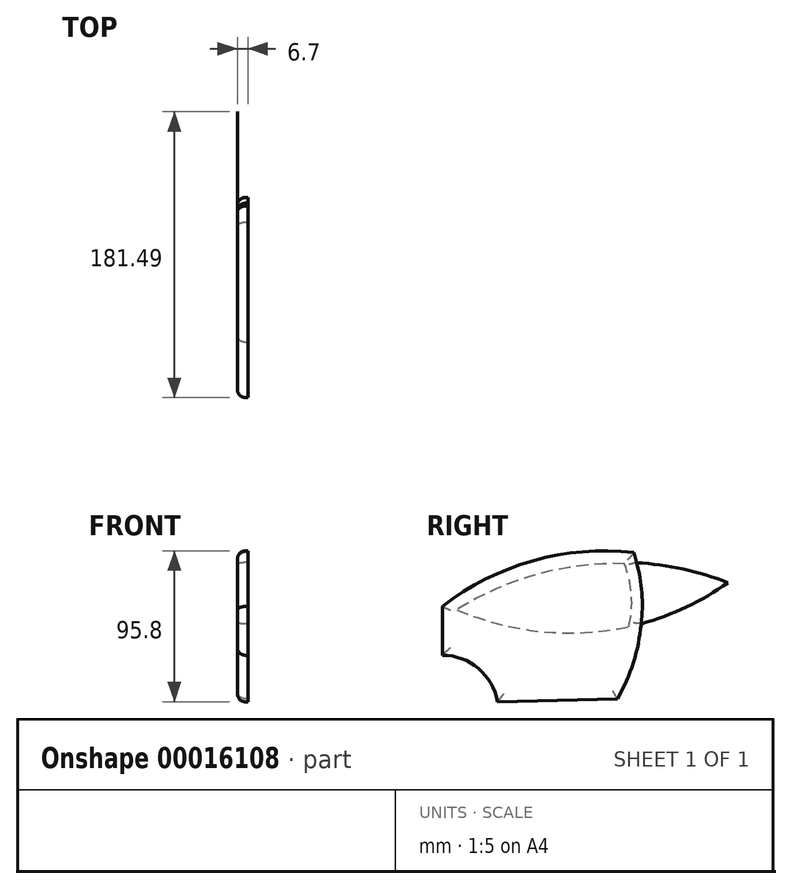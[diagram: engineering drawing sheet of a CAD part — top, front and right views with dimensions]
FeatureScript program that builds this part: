
annotation { "Feature Type Name" : "Feature", "Feature Type Description" : "" }
export const myFeature = defineFeature(function(context is Context, id is Id, definition is map)
    precondition{}
    {
        {
            var Q0;
            Q0=qCreatedBy(makeId("Right.planeOp"),FACE);
            var sketch = newSketch(context, id + "F0", { "sketchPlane" : qUnion([Q0])});
            skArc(sketch, "E0", {"start": v(39.4, 40.65) * mm, "mid": v(-24.74, 35.47) * mm, "end": v(-82.2, 6.49) * mm});
            skArc(sketch, "E1", {"start": v(-47.13, -54.09) * mm, "mid": v(-59.3, -32.92) * mm, "end": v(-82.2, -24.48) * mm});
            skLineSegment(sketch, "E2", {"start": v(-82.2, 6.94) * mm, "end": v(-82.2, -24.48) * mm});
            skLineSegment(sketch, "E3", {"start": v(-47.13, -54.09) * mm, "end": v(29.03, -52.2) * mm});
            skArc(sketch, "E4", {"start": v(29.03, -52.2) * mm, "mid": v(39.1, -29.18) * mm, "end": v(44.1, -4.55) * mm});
            skArc(sketch, "E5", {"start": v(41.16, 34.32) * mm, "mid": v(40.37, 37.5) * mm, "end": v(39.4, 40.65) * mm});
            skArc(sketch, "E6", {"start": v(44.1, -4.55) * mm, "mid": v(44.55, 15.03) * mm, "end": v(41.16, 34.32) * mm});
            skSolve(sketch);
        }
        {
            var Q0;
            Q0=qCreatedBy(makeId("Right.planeOp"),FACE);
            var sketch = newSketch(context, id + "F1", { "sketchPlane" : qUnion([Q0])});
            skArc(sketch, "E7", {"start": v(33.51, 33.61) * mm, "mid": v(-21.9, 26.86) * mm, "end": v(-72.98, 4.39) * mm});
            skArc(sketch, "E8", {"start": v(-72.98, 4.39) * mm, "mid": v(-19.22, -9.5) * mm, "end": v(36.21, -6.46) * mm});
            skArc(sketch, "E9", {"start": v(36.21, -6.46) * mm, "mid": v(37.93, 13.79) * mm, "end": v(33.51, 33.61) * mm});
            skArc(sketch, "E10", {"start": v(43.96, -4.5) * mm, "mid": v(44.38, 15) * mm, "end": v(41, 34.2) * mm});
            skArc(sketch, "E11", {"start": v(99.3, 21.57) * mm, "mid": v(70.66, 30.25) * mm, "end": v(41, 34.2) * mm});
            skArc(sketch, "E12", {"start": v(43.96, -4.5) * mm, "mid": v(72.78, 6.09) * mm, "end": v(99.3, 21.57) * mm});
            skSolve(sketch);
        }
        {
            var Q0;
            Q0=makeQuery(id+"F1.imprint","IMPRINT",FACE,{"disambiguationData":[TD([[makeQuery(id+"F1.imprint","IMPRINT",EDGE,{"derivedFrom":sQuery(id+"F1.wireOp",EDGE,"E7")}),1.0]])]});
            var Q1;
            Q1=makeQuery(id+"F1.imprint","IMPRINT",FACE,{"disambiguationData":[TD([[makeQuery(id+"F1.imprint","IMPRINT",EDGE,{"derivedFrom":sQuery(id+"F1.wireOp",EDGE,"E10")}),-1.0]])]});
            extrude(context, id + "F2", {"entities" : qUnion([Q0, Q1]), "depth" : 0.26 * mm});
        }
        {
            var Q0;
            {var subQ2=sQuery(id+"F0.wireOp",EDGE,"E0");Q0=makeQuery(id+"F0.imprint","IMPRINT",FACE,{"disambiguationData":[TD([[makeQuery(id+"F0.imprint","IMPRINT",EDGE,{"derivedFrom":subQ2}),1.0]])]});}
            extrude(context, id + "F3", {"entities" : qUnion([Q0]), "depth" : 6.7 * mm});
        }
        {
            var Q0;
            Q0=makeQuery(id+"F3.opExtrude","CAP_FACE",FACE,{"disambiguationData":[OSD([sQuery(id+"F0.wireOp",EDGE,"E0"),sQuery(id+"F0.wireOp",EDGE,"E1"),sQuery(id+"F0.wireOp",EDGE,"E2"),sQuery(id+"F0.wireOp",EDGE,"E3"),sQuery(id+"F0.wireOp",EDGE,"E4"),sQuery(id+"F0.wireOp",EDGE,"E5"),sQuery(id+"F0.wireOp",EDGE,"E6")])],"isStart":true});
            fillet(context, id + "F4", {"entities" : qUnion([Q0]), "radius" : 5.08 * mm, "tangentPropagation" : true, "allowEdgeOverflow" : false});
        }
    });
